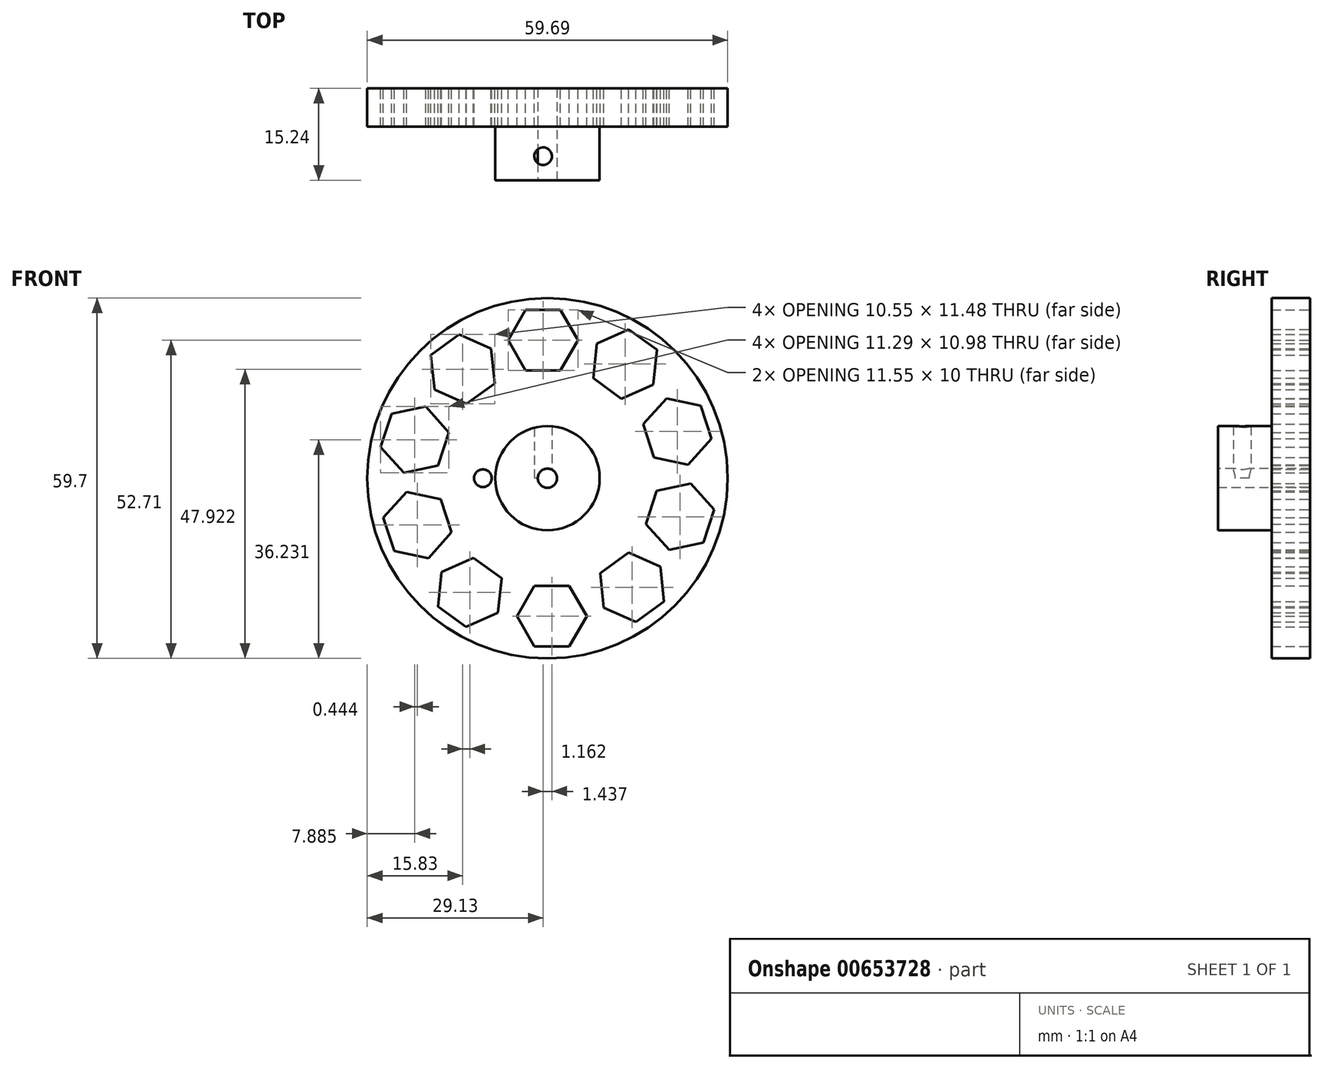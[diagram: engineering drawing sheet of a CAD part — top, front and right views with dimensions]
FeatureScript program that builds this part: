
annotation { "Feature Type Name" : "Feature", "Feature Type Description" : "" }
export const myFeature = defineFeature(function(context is Context, id is Id, definition is map)
    precondition{}
    {
        {
            var Q0;
            Q0=qCreatedBy(makeId("Front.planeOp"),FACE);
            var sketch = newSketch(context, id + "F0", { "sketchPlane" : qUnion([Q0])});
            skCircle(sketch, "E0.cCircle", {"center": v(0, 22.86) * mm, "radius": 5 * mm, "construction": true});
            skLineSegment(sketch, "E0.0", {"start": v(2.89, 17.86) * mm, "end": v(-2.89, 17.86) * mm});
            skLineSegment(sketch, "E0.1", {"start": v(-2.89, 17.86) * mm, "end": v(-5.77, 22.86) * mm});
            skLineSegment(sketch, "E0.2", {"start": v(-5.77, 22.86) * mm, "end": v(-2.89, 27.86) * mm});
            skLineSegment(sketch, "E0.3", {"start": v(-2.89, 27.86) * mm, "end": v(2.89, 27.86) * mm});
            skLineSegment(sketch, "E0.4", {"start": v(2.89, 27.86) * mm, "end": v(5.77, 22.86) * mm});
            skLineSegment(sketch, "E0.5", {"start": v(5.77, 22.86) * mm, "end": v(2.89, 17.86) * mm});
            skPoint(sketch, "E0.0.midPoint", {"position": v(0, 17.86) * mm});
            skPoint(sketch, "E1", {"position": v(0, 27.86) * mm});
            skCircle(sketch, "E2.1.0", {"center": v(-13.3, 18.07) * mm, "radius": 5 * mm, "construction": true});
            skLineSegment(sketch, "E2.1.1", {"start": v(-13.9, 23.81) * mm, "end": v(-8.63, 21.47) * mm});
            skLineSegment(sketch, "E2.1.2", {"start": v(-18.57, 20.42) * mm, "end": v(-13.9, 23.81) * mm});
            skLineSegment(sketch, "E2.1.3", {"start": v(-17.97, 14.68) * mm, "end": v(-18.57, 20.42) * mm});
            skLineSegment(sketch, "E2.1.4", {"start": v(-12.7, 12.33) * mm, "end": v(-17.97, 14.68) * mm});
            skLineSegment(sketch, "E2.1.5", {"start": v(-8.03, 15.72) * mm, "end": v(-12.7, 12.33) * mm});
            skLineSegment(sketch, "E2.1.6", {"start": v(-8.63, 21.47) * mm, "end": v(-8.03, 15.72) * mm});
            skCircle(sketch, "E2.2.0", {"center": v(-21.24, 6.38) * mm, "radius": 5 * mm, "construction": true});
            skLineSegment(sketch, "E2.2.1", {"start": v(-25.1, 10.67) * mm, "end": v(-19.46, 11.87) * mm});
            skLineSegment(sketch, "E2.2.2", {"start": v(-26.9, 5.18) * mm, "end": v(-25.1, 10.67) * mm});
            skLineSegment(sketch, "E2.2.3", {"start": v(-23.03, 0.9) * mm, "end": v(-26.9, 5.18) * mm});
            skLineSegment(sketch, "E2.2.4", {"start": v(-17.38, 2.1) * mm, "end": v(-23.03, 0.9) * mm});
            skLineSegment(sketch, "E2.2.5", {"start": v(-15.6, 7.58) * mm, "end": v(-17.38, 2.1) * mm});
            skLineSegment(sketch, "E2.2.6", {"start": v(-19.46, 11.87) * mm, "end": v(-15.6, 7.58) * mm});
            skCircle(sketch, "E2.3.0", {"center": v(-20.8, -7.75) * mm, "radius": 5 * mm, "construction": true});
            skLineSegment(sketch, "E2.3.1", {"start": v(-26.45, -6.55) * mm, "end": v(-22.59, -2.26) * mm});
            skLineSegment(sketch, "E2.3.2", {"start": v(-24.66, -12.04) * mm, "end": v(-26.45, -6.55) * mm});
            skLineSegment(sketch, "E2.3.3", {"start": v(-19.02, -13.24) * mm, "end": v(-24.66, -12.04) * mm});
            skLineSegment(sketch, "E2.3.4", {"start": v(-15.15, -8.95) * mm, "end": v(-19.02, -13.24) * mm});
            skLineSegment(sketch, "E2.3.5", {"start": v(-16.94, -3.46) * mm, "end": v(-15.15, -8.95) * mm});
            skLineSegment(sketch, "E2.3.6", {"start": v(-22.59, -2.26) * mm, "end": v(-16.94, -3.46) * mm});
            skCircle(sketch, "E2.4.0", {"center": v(-12.14, -18.92) * mm, "radius": 5 * mm, "construction": true});
            skLineSegment(sketch, "E2.4.1", {"start": v(-17.41, -21.26) * mm, "end": v(-16.8, -15.52) * mm});
            skLineSegment(sketch, "E2.4.2", {"start": v(-12.74, -24.66) * mm, "end": v(-17.41, -21.26) * mm});
            skLineSegment(sketch, "E2.4.3", {"start": v(-7.47, -22.3) * mm, "end": v(-12.74, -24.66) * mm});
            skLineSegment(sketch, "E2.4.4", {"start": v(-6.86, -16.57) * mm, "end": v(-7.47, -22.3) * mm});
            skLineSegment(sketch, "E2.4.5", {"start": v(-11.53, -13.17) * mm, "end": v(-6.86, -16.57) * mm});
            skLineSegment(sketch, "E2.4.6", {"start": v(-16.8, -15.52) * mm, "end": v(-11.53, -13.17) * mm});
            skCircle(sketch, "E2.5.0", {"center": v(1.44, -22.86) * mm, "radius": 5 * mm, "construction": true});
            skLineSegment(sketch, "E2.5.1", {"start": v(-1.45, -27.86) * mm, "end": v(-4.34, -22.86) * mm});
            skLineSegment(sketch, "E2.5.2", {"start": v(4.32, -27.86) * mm, "end": v(-1.45, -27.86) * mm});
            skLineSegment(sketch, "E2.5.3", {"start": v(7.21, -22.86) * mm, "end": v(4.32, -27.86) * mm});
            skLineSegment(sketch, "E2.5.4", {"start": v(4.32, -17.86) * mm, "end": v(7.21, -22.86) * mm});
            skLineSegment(sketch, "E2.5.5", {"start": v(-1.45, -17.86) * mm, "end": v(4.32, -17.86) * mm});
            skLineSegment(sketch, "E2.5.6", {"start": v(-4.34, -22.86) * mm, "end": v(-1.45, -17.86) * mm});
            skCircle(sketch, "E2.6.0", {"center": v(14.74, -18.07) * mm, "radius": 5 * mm, "construction": true});
            skLineSegment(sketch, "E2.6.1", {"start": v(15.34, -23.81) * mm, "end": v(10.07, -21.47) * mm});
            skLineSegment(sketch, "E2.6.2", {"start": v(20.01, -20.42) * mm, "end": v(15.34, -23.81) * mm});
            skLineSegment(sketch, "E2.6.3", {"start": v(19.4, -14.68) * mm, "end": v(20.01, -20.42) * mm});
            skLineSegment(sketch, "E2.6.4", {"start": v(14.13, -12.33) * mm, "end": v(19.4, -14.68) * mm});
            skLineSegment(sketch, "E2.6.5", {"start": v(9.46, -15.72) * mm, "end": v(14.13, -12.33) * mm});
            skLineSegment(sketch, "E2.6.6", {"start": v(10.07, -21.47) * mm, "end": v(9.46, -15.72) * mm});
            skCircle(sketch, "E2.7.0", {"center": v(22.68, -6.38) * mm, "radius": 5 * mm, "construction": true});
            skLineSegment(sketch, "E2.7.1", {"start": v(26.54, -10.67) * mm, "end": v(20.9, -11.87) * mm});
            skLineSegment(sketch, "E2.7.2", {"start": v(28.33, -5.18) * mm, "end": v(26.54, -10.67) * mm});
            skLineSegment(sketch, "E2.7.3", {"start": v(24.47, -0.9) * mm, "end": v(28.33, -5.18) * mm});
            skLineSegment(sketch, "E2.7.4", {"start": v(18.82, -2.1) * mm, "end": v(24.47, -0.9) * mm});
            skLineSegment(sketch, "E2.7.5", {"start": v(17.03, -7.58) * mm, "end": v(18.82, -2.1) * mm});
            skLineSegment(sketch, "E2.7.6", {"start": v(20.9, -11.87) * mm, "end": v(17.03, -7.58) * mm});
            skCircle(sketch, "E2.8.0", {"center": v(22.24, 7.75) * mm, "radius": 5 * mm, "construction": true});
            skLineSegment(sketch, "E2.8.1", {"start": v(27.88, 6.55) * mm, "end": v(24.02, 2.26) * mm});
            skLineSegment(sketch, "E2.8.2", {"start": v(26.1, 12.04) * mm, "end": v(27.88, 6.55) * mm});
            skLineSegment(sketch, "E2.8.3", {"start": v(20.45, 13.24) * mm, "end": v(26.1, 12.04) * mm});
            skLineSegment(sketch, "E2.8.4", {"start": v(16.6, 8.95) * mm, "end": v(20.45, 13.24) * mm});
            skLineSegment(sketch, "E2.8.5", {"start": v(18.37, 3.46) * mm, "end": v(16.6, 8.95) * mm});
            skLineSegment(sketch, "E2.8.6", {"start": v(24.02, 2.26) * mm, "end": v(18.37, 3.46) * mm});
            skCircle(sketch, "E2.9.0", {"center": v(13.57, 18.92) * mm, "radius": 5 * mm, "construction": true});
            skLineSegment(sketch, "E2.9.1", {"start": v(18.85, 21.26) * mm, "end": v(18.24, 15.52) * mm});
            skLineSegment(sketch, "E2.9.2", {"start": v(14.18, 24.66) * mm, "end": v(18.85, 21.26) * mm});
            skLineSegment(sketch, "E2.9.3", {"start": v(8.9, 22.3) * mm, "end": v(14.18, 24.66) * mm});
            skLineSegment(sketch, "E2.9.4", {"start": v(8.3, 16.57) * mm, "end": v(8.9, 22.3) * mm});
            skLineSegment(sketch, "E2.9.5", {"start": v(12.97, 13.17) * mm, "end": v(8.3, 16.57) * mm});
            skLineSegment(sketch, "E2.9.6", {"start": v(18.24, 15.52) * mm, "end": v(12.97, 13.17) * mm});
            skPoint(sketch, "E2.center", {"position": v(0.72, 0) * mm});
            skCircle(sketch, "E3", {"center": v(0.72, 0) * mm, "radius": 29.85 * mm});
            skSolve(sketch);
        }
        {
            var Q0;
            Q0=makeQuery(id+"F0.imprint","IMPRINT",FACE,{"disambiguationData":[TD([[makeQuery(id+"F0.imprint","IMPRINT",EDGE,{"derivedFrom":sQuery(id+"F0.wireOp",EDGE,"E0.0")}),1.0]])]});
            extrude(context, id + "F1", {"entities" : qUnion([Q0]), "depth" : 6.35 * mm, "offsetDistance" : 25.4 * mm});
        }
        {
            var Q0;
            Q0=makeQuery(id+"F1.opExtrude","CAP_FACE",FACE,{"disambiguationData":[OSD([sQuery(id+"F0.wireOp",EDGE,"E0.0"),sQuery(id+"F0.wireOp",EDGE,"E0.1"),sQuery(id+"F0.wireOp",EDGE,"E0.2"),sQuery(id+"F0.wireOp",EDGE,"E0.3"),sQuery(id+"F0.wireOp",EDGE,"E0.4"),sQuery(id+"F0.wireOp",EDGE,"E0.5"),sQuery(id+"F0.wireOp",EDGE,"E2.1.1"),sQuery(id+"F0.wireOp",EDGE,"E2.1.2"),sQuery(id+"F0.wireOp",EDGE,"E2.1.3"),sQuery(id+"F0.wireOp",EDGE,"E2.1.4"),sQuery(id+"F0.wireOp",EDGE,"E2.1.5"),sQuery(id+"F0.wireOp",EDGE,"E2.1.6"),sQuery(id+"F0.wireOp",EDGE,"E2.2.1"),sQuery(id+"F0.wireOp",EDGE,"E2.2.2"),sQuery(id+"F0.wireOp",EDGE,"E2.2.3"),sQuery(id+"F0.wireOp",EDGE,"E2.2.4"),sQuery(id+"F0.wireOp",EDGE,"E2.2.5"),sQuery(id+"F0.wireOp",EDGE,"E2.2.6"),sQuery(id+"F0.wireOp",EDGE,"E2.3.1"),sQuery(id+"F0.wireOp",EDGE,"E2.3.2"),sQuery(id+"F0.wireOp",EDGE,"E2.3.3"),sQuery(id+"F0.wireOp",EDGE,"E2.3.4"),sQuery(id+"F0.wireOp",EDGE,"E2.3.5"),sQuery(id+"F0.wireOp",EDGE,"E2.3.6"),sQuery(id+"F0.wireOp",EDGE,"E2.4.1"),sQuery(id+"F0.wireOp",EDGE,"E2.4.2"),sQuery(id+"F0.wireOp",EDGE,"E2.4.3"),sQuery(id+"F0.wireOp",EDGE,"E2.4.4"),sQuery(id+"F0.wireOp",EDGE,"E2.4.5"),sQuery(id+"F0.wireOp",EDGE,"E2.4.6"),sQuery(id+"F0.wireOp",EDGE,"E2.5.1"),sQuery(id+"F0.wireOp",EDGE,"E2.5.2"),sQuery(id+"F0.wireOp",EDGE,"E2.5.3"),sQuery(id+"F0.wireOp",EDGE,"E2.5.4"),sQuery(id+"F0.wireOp",EDGE,"E2.5.5"),sQuery(id+"F0.wireOp",EDGE,"E2.5.6"),sQuery(id+"F0.wireOp",EDGE,"E2.6.1"),sQuery(id+"F0.wireOp",EDGE,"E2.6.2"),sQuery(id+"F0.wireOp",EDGE,"E2.6.3"),sQuery(id+"F0.wireOp",EDGE,"E2.6.4"),sQuery(id+"F0.wireOp",EDGE,"E2.6.5"),sQuery(id+"F0.wireOp",EDGE,"E2.6.6"),sQuery(id+"F0.wireOp",EDGE,"E2.7.1"),sQuery(id+"F0.wireOp",EDGE,"E2.7.2"),sQuery(id+"F0.wireOp",EDGE,"E2.7.3"),sQuery(id+"F0.wireOp",EDGE,"E2.7.4"),sQuery(id+"F0.wireOp",EDGE,"E2.7.5"),sQuery(id+"F0.wireOp",EDGE,"E2.7.6"),sQuery(id+"F0.wireOp",EDGE,"E2.8.1"),sQuery(id+"F0.wireOp",EDGE,"E2.8.2"),sQuery(id+"F0.wireOp",EDGE,"E2.8.3"),sQuery(id+"F0.wireOp",EDGE,"E2.8.4"),sQuery(id+"F0.wireOp",EDGE,"E2.8.5"),sQuery(id+"F0.wireOp",EDGE,"E2.8.6"),sQuery(id+"F0.wireOp",EDGE,"E2.9.1"),sQuery(id+"F0.wireOp",EDGE,"E2.9.2"),sQuery(id+"F0.wireOp",EDGE,"E2.9.3"),sQuery(id+"F0.wireOp",EDGE,"E2.9.4"),sQuery(id+"F0.wireOp",EDGE,"E2.9.5"),sQuery(id+"F0.wireOp",EDGE,"E2.9.6"),sQuery(id+"F0.wireOp",EDGE,"E3")])],"isStart":false});
            var sketch = newSketch(context, id + "F2", { "sketchPlane" : qUnion([Q0])});
            skCircle(sketch, "E4.0.0", {"center": v(0.72, 0) * mm, "radius": 29.85 * mm});
            skCircle(sketch, "E5", {"center": v(0.72, 0) * mm, "radius": 8.64 * mm});
            skSolve(sketch);
        }
        {
            var Q0;
            Q0=makeQuery(id+"F2.imprint","IMPRINT",FACE,{"disambiguationData":[TD([[makeQuery(id+"F2.imprint","IMPRINT",EDGE,{"derivedFrom":sQuery(id+"F2.wireOp",EDGE,"E5")}),1.0]])]});
            extrude(context, id + "F3", {"entities" : qUnion([Q0]), "operationType" : NewBodyOperationType.ADD, "depth" : 8.9 * mm, "offsetDistance" : 25.4 * mm});
        }
        {
            var Q0;
            Q0=makeQuery(id+"F3.opExtrude","CAP_FACE",FACE,{"disambiguationData":[OSD([sQuery(id+"F2.wireOp",EDGE,"E5")])],"isStart":false});
            var sketch = newSketch(context, id + "F4", { "sketchPlane" : qUnion([Q0])});
            skCircle(sketch, "E6.0.0", {"center": v(0.72, 0) * mm, "radius": 8.64 * mm});
            skCircle(sketch, "E7", {"center": v(0.72, 0) * mm, "radius": 1.59 * mm});
            skSolve(sketch);
        }
        {
            var Q0;
            Q0=makeQuery(id+"F4.imprint","IMPRINT",FACE,{"disambiguationData":[TD([[makeQuery(id+"F4.imprint","IMPRINT",EDGE,{"derivedFrom":sQuery(id+"F4.wireOp",EDGE,"E7")}),1.0]])]});
            extrude(context, id + "F5", {"entities" : qUnion([Q0]), "operationType" : NewBodyOperationType.REMOVE, "endBound" : BoundingType.THROUGH_ALL, "oppositeDirection" : true, "depth" : 25.4 * mm, "offsetDistance" : 25.4 * mm});
        }
        {
            var Q0;
            Q0=makeQuery(id+"F1.opExtrude","CAP_FACE",FACE,{"disambiguationData":[OSD([sQuery(id+"F0.wireOp",EDGE,"E0.0"),sQuery(id+"F0.wireOp",EDGE,"E0.1"),sQuery(id+"F0.wireOp",EDGE,"E0.2"),sQuery(id+"F0.wireOp",EDGE,"E0.3"),sQuery(id+"F0.wireOp",EDGE,"E0.4"),sQuery(id+"F0.wireOp",EDGE,"E0.5"),sQuery(id+"F0.wireOp",EDGE,"E2.1.1"),sQuery(id+"F0.wireOp",EDGE,"E2.1.2"),sQuery(id+"F0.wireOp",EDGE,"E2.1.3"),sQuery(id+"F0.wireOp",EDGE,"E2.1.4"),sQuery(id+"F0.wireOp",EDGE,"E2.1.5"),sQuery(id+"F0.wireOp",EDGE,"E2.1.6"),sQuery(id+"F0.wireOp",EDGE,"E2.2.1"),sQuery(id+"F0.wireOp",EDGE,"E2.2.2"),sQuery(id+"F0.wireOp",EDGE,"E2.2.3"),sQuery(id+"F0.wireOp",EDGE,"E2.2.4"),sQuery(id+"F0.wireOp",EDGE,"E2.2.5"),sQuery(id+"F0.wireOp",EDGE,"E2.2.6"),sQuery(id+"F0.wireOp",EDGE,"E2.3.1"),sQuery(id+"F0.wireOp",EDGE,"E2.3.2"),sQuery(id+"F0.wireOp",EDGE,"E2.3.3"),sQuery(id+"F0.wireOp",EDGE,"E2.3.4"),sQuery(id+"F0.wireOp",EDGE,"E2.3.5"),sQuery(id+"F0.wireOp",EDGE,"E2.3.6"),sQuery(id+"F0.wireOp",EDGE,"E2.4.1"),sQuery(id+"F0.wireOp",EDGE,"E2.4.2"),sQuery(id+"F0.wireOp",EDGE,"E2.4.3"),sQuery(id+"F0.wireOp",EDGE,"E2.4.4"),sQuery(id+"F0.wireOp",EDGE,"E2.4.5"),sQuery(id+"F0.wireOp",EDGE,"E2.4.6"),sQuery(id+"F0.wireOp",EDGE,"E2.5.1"),sQuery(id+"F0.wireOp",EDGE,"E2.5.2"),sQuery(id+"F0.wireOp",EDGE,"E2.5.3"),sQuery(id+"F0.wireOp",EDGE,"E2.5.4"),sQuery(id+"F0.wireOp",EDGE,"E2.5.5"),sQuery(id+"F0.wireOp",EDGE,"E2.5.6"),sQuery(id+"F0.wireOp",EDGE,"E2.6.1"),sQuery(id+"F0.wireOp",EDGE,"E2.6.2"),sQuery(id+"F0.wireOp",EDGE,"E2.6.3"),sQuery(id+"F0.wireOp",EDGE,"E2.6.4"),sQuery(id+"F0.wireOp",EDGE,"E2.6.5"),sQuery(id+"F0.wireOp",EDGE,"E2.6.6"),sQuery(id+"F0.wireOp",EDGE,"E2.7.1"),sQuery(id+"F0.wireOp",EDGE,"E2.7.2"),sQuery(id+"F0.wireOp",EDGE,"E2.7.3"),sQuery(id+"F0.wireOp",EDGE,"E2.7.4"),sQuery(id+"F0.wireOp",EDGE,"E2.7.5"),sQuery(id+"F0.wireOp",EDGE,"E2.7.6"),sQuery(id+"F0.wireOp",EDGE,"E2.8.1"),sQuery(id+"F0.wireOp",EDGE,"E2.8.2"),sQuery(id+"F0.wireOp",EDGE,"E2.8.3"),sQuery(id+"F0.wireOp",EDGE,"E2.8.4"),sQuery(id+"F0.wireOp",EDGE,"E2.8.5"),sQuery(id+"F0.wireOp",EDGE,"E2.8.6"),sQuery(id+"F0.wireOp",EDGE,"E2.9.1"),sQuery(id+"F0.wireOp",EDGE,"E2.9.2"),sQuery(id+"F0.wireOp",EDGE,"E2.9.3"),sQuery(id+"F0.wireOp",EDGE,"E2.9.4"),sQuery(id+"F0.wireOp",EDGE,"E2.9.5"),sQuery(id+"F0.wireOp",EDGE,"E2.9.6"),sQuery(id+"F0.wireOp",EDGE,"E3")])],"isStart":true});
            var sketch = newSketch(context, id + "F6", { "sketchPlane" : qUnion([Q0])});
            skCircle(sketch, "E8", {"center": v(9.97, 0) * mm, "radius": 1.46 * mm});
            skSolve(sketch);
        }
        {
            var Q0;
            Q0=makeQuery(id+"F6.imprint","IMPRINT",FACE,{"disambiguationData":[TD([[makeQuery(id+"F6.imprint","IMPRINT",EDGE,{"derivedFrom":sQuery(id+"F6.wireOp",EDGE,"E8")}),1.0]])]});
            var Q1;
            Q1=sQuery(id+"F6.wireOp",EDGE,"E8");
            extrude(context, id + "F7", {"entities" : qUnion([Q0]), "operationType" : NewBodyOperationType.REMOVE, "surfaceEntities" : qUnion([Q1]), "endBound" : BoundingType.THROUGH_ALL, "oppositeDirection" : true, "depth" : 25.4 * mm, "offsetDistance" : 25.4 * mm});
        }
        {
            var Q0;
            Q0=qCreatedBy(makeId("Top.planeOp"),FACE);
            var sketch = newSketch(context, id + "F8", { "sketchPlane" : qUnion([Q0])});
            skCircle(sketch, "E9", {"center": v(0, -11.24) * mm, "radius": 1.46 * mm});
            skSolve(sketch);
        }
        {
            var Q0;
            Q0 = qSketchRegion(id + "F8", true);
            extrude(context, id + "F9", {"entities" : qUnion([Q0]), "operationType" : NewBodyOperationType.REMOVE, "endBound" : BoundingType.THROUGH_ALL, "depth" : 25.4 * mm, "offsetDistance" : 25.4 * mm});
        }
    });
